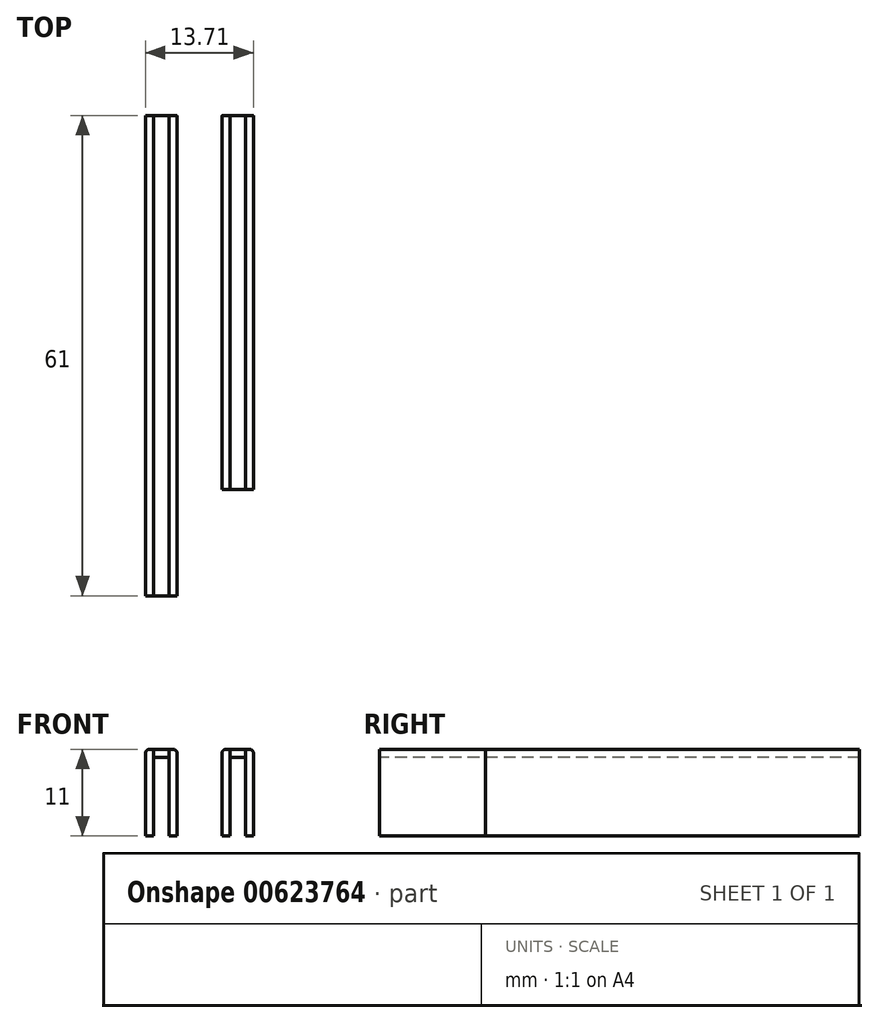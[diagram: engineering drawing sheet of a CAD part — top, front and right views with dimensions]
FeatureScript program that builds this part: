
annotation { "Feature Type Name" : "Feature", "Feature Type Description" : "" }
export const myFeature = defineFeature(function(context is Context, id is Id, definition is map)
    precondition{}
    {
        {
            var Q0;
            Q0=qCreatedBy(makeId("Top.planeOp"),FACE);
            var sketch = newSketch(context, id + "F0", { "sketchPlane" : qUnion([Q0])});
            skLineSegment(sketch, "E0.bottom", {"start": v(0, 0) * mm, "end": v(2, 0) * mm});
            skLineSegment(sketch, "E0.top", {"start": v(0, -61) * mm, "end": v(2, -61) * mm});
            skLineSegment(sketch, "E0.left", {"start": v(0, 0) * mm, "end": v(0, -61) * mm});
            skLineSegment(sketch, "E0.right", {"start": v(2, 0) * mm, "end": v(2, -61) * mm});
            skLineSegment(sketch, "E1.bottom", {"start": v(2, 0) * mm, "end": v(3, 0) * mm});
            skLineSegment(sketch, "E1.top", {"start": v(2, -61) * mm, "end": v(3, -61) * mm});
            skLineSegment(sketch, "E1.right", {"start": v(3, 0) * mm, "end": v(3, -61) * mm});
            skLineSegment(sketch, "E2.bottom", {"start": v(0, -61) * mm, "end": v(-1, -61) * mm});
            skLineSegment(sketch, "E2.top", {"start": v(0, 0) * mm, "end": v(-1, 0) * mm});
            skLineSegment(sketch, "E2.left", {"start": v(0, -61) * mm, "end": v(0, 0) * mm});
            skLineSegment(sketch, "E2.right", {"start": v(-1, -61) * mm, "end": v(-1, 0) * mm});
            skLineSegment(sketch, "E3.bottom", {"start": v(9.7, 0) * mm, "end": v(11.7, 0) * mm});
            skLineSegment(sketch, "E3.top", {"start": v(9.7, -47.5) * mm, "end": v(11.7, -47.5) * mm});
            skLineSegment(sketch, "E3.left", {"start": v(9.7, 0) * mm, "end": v(9.7, -47.5) * mm});
            skLineSegment(sketch, "E3.right", {"start": v(11.7, 0) * mm, "end": v(11.7, -47.5) * mm});
            skLineSegment(sketch, "E4.bottom", {"start": v(9.7, 0) * mm, "end": v(8.7, 0) * mm});
            skLineSegment(sketch, "E4.top", {"start": v(9.7, -47.5) * mm, "end": v(8.7, -47.5) * mm});
            skLineSegment(sketch, "E4.right", {"start": v(8.7, 0) * mm, "end": v(8.7, -47.5) * mm});
            skLineSegment(sketch, "E5.bottom", {"start": v(11.7, 0) * mm, "end": v(12.7, 0) * mm});
            skLineSegment(sketch, "E5.top", {"start": v(11.7, -47.5) * mm, "end": v(12.7, -47.5) * mm});
            skLineSegment(sketch, "E5.right", {"start": v(12.7, 0) * mm, "end": v(12.7, -47.5) * mm});
            skSolve(sketch);
        }
        {
            var Q0;
            Q0=makeQuery(id+"F0.imprint","IMPRINT",FACE,{"disambiguationData":[TD([[makeQuery(id+"F0.imprint","IMPRINT",EDGE,{"derivedFrom":sQuery(id+"F0.wireOp",EDGE,"E0.bottom")}),-1.0]])]});
            var Q1;
            Q1=makeQuery(id+"F0.imprint","IMPRINT",FACE,{"disambiguationData":[TD([[makeQuery(id+"F0.imprint","IMPRINT",EDGE,{"derivedFrom":sQuery(id+"F0.wireOp",EDGE,"E3.bottom")}),-1.0]])]});
            extrude(context, id + "F1", {"entities" : qUnion([Q0, Q1]), "oppositeDirection" : true, "depth" : 1 * mm, "offsetDistance" : 25 * mm});
        }
        {
            var Q0;
            Q0=makeQuery(id+"F0.imprint","IMPRINT",FACE,{"disambiguationData":[TD([[makeQuery(id+"F0.imprint","IMPRINT",EDGE,{"derivedFrom":sQuery(id+"F0.wireOp",EDGE,"E1.bottom")}),-1.0]])]});
            var Q1;
            Q1=makeQuery(id+"F0.imprint","IMPRINT",FACE,{"disambiguationData":[TD([[makeQuery(id+"F0.imprint","IMPRINT",EDGE,{"derivedFrom":sQuery(id+"F0.wireOp",EDGE,"E4.bottom")}),1.0]])]});
            var Q2;
            Q2=makeQuery(id+"F0.imprint","IMPRINT",FACE,{"disambiguationData":[TD([[makeQuery(id+"F0.imprint","IMPRINT",EDGE,{"derivedFrom":sQuery(id+"F0.wireOp",EDGE,"E5.bottom")}),-1.0]])]});
            var Q3;
            Q3=makeQuery(id+"F0.imprint","IMPRINT",FACE,{"disambiguationData":[TD([[makeQuery(id+"F0.imprint","IMPRINT",EDGE,{"derivedFrom":sQuery(id+"F0.wireOp",EDGE,"E2.bottom")}),-1.0]])]});
            extrude(context, id + "F2", {"entities" : qUnion([Q0, Q1, Q2, Q3]), "oppositeDirection" : true, "depth" : 11 * mm, "offsetDistance" : 25 * mm});
        }
        {
            var Q0;
            Q0=makeQuery(id+"F2.opExtrude","CAP_EDGE",EDGE,{"disambiguationData":[OSD([sQuery(id+"F0.wireOp",EDGE,"E2.right")])],"isStart":true});
            var Q1;
            Q1=makeQuery(id+"F2.opExtrude","CAP_EDGE",EDGE,{"disambiguationData":[OSD([sQuery(id+"F0.wireOp",EDGE,"E1.right")])],"isStart":true});
            var Q2;
            Q2=makeQuery(id+"F2.opExtrude","CAP_EDGE",EDGE,{"disambiguationData":[OSD([sQuery(id+"F0.wireOp",EDGE,"E4.right")])],"isStart":true});
            var Q3;
            Q3=makeQuery(id+"F2.opExtrude","CAP_EDGE",EDGE,{"disambiguationData":[OSD([sQuery(id+"F0.wireOp",EDGE,"E5.right")])],"isStart":true});
            fillet(context, id + "F3", {"entities" : qUnion([Q0, Q1, Q2, Q3]), "radius" : .5 * mm, "tangentPropagation" : true, "allowEdgeOverflow" : false});
        }
    });
